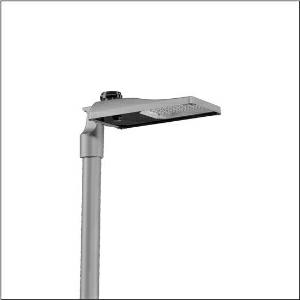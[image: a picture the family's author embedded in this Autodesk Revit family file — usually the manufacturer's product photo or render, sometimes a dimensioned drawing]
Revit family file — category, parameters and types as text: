
# Revit family: streetlight_sl_31_mini___st1_0a_5xh6d35m08ha_c080
name_source: partatom
category: Lighting Fixtures
units: mm (PartAtom-declared; Revit-internal decimal feet)

## family parameters
Cut with Voids When Loaded = No
Host = Face
Light Source = No
Part Type = Normal
Room Calculation Point = No
Round Connector Dimension = Use Diameter
Shared = No

## types (1)
- --- (1 x LED, 9230 lm, 68.3 W, 3000K)
    Apparent Load = 68 VA
    CIE Flux Codes = 37 72 97 100 100
    Color Rendering = 70
    Color Temperature = 3000K
    Default Elevation = 1800 mm
    Description = Streetlight SL 31 mini NEMA (7pin), Desk-Remote mast luminaire for post-top, side-entry; light control with lens of PMMA; light distribution: ST1.0a, direct asymmetric distribution, for standard-compliant lighting for roads and squares; LED: luminous flux: 9.230lm, light colour: 730, colour temperature: 3000K; luminous efficacy: 135,1lm/W; control: pre-setting: linear dimming characteristic, flexible luminous flux parameterisation, time-dependent luminous flux control, constant luminous flux control, intelligent temperature release in ECG and LED module, overheat protection; luminaire housing, of diecast aluminium, SITECO metallic grey (DB 702S), corrosivity category C5 high according to DIN EN ISO 12944; cover of toughened safety glass, transparent, opened without tools; mast flange of diecast aluminium, SITECO metallic grey (DB 702S), spigot size: 76/60mm, mast flange included unmounted; cable length: 8,5m, connection cable pre-assembled; mains connection: 220..240V, AC, 50/60Hz; power consumption (at start of service life): 68,3W / (at end of service life): 74,5W / (with reduced operation 50%): 29,5W; protection rating (complete): IP66; insulation class (complete): insulation class I (protective earthing); impact resistance: IK09; certification: CE, ENEC, ENEC+, VDE, UKCA; permissible operating ambient temperature for outdoor applications: -40..+50°C; packaging unit: 1 piece

Light Distribution: ST1.0a
    Height = 76 mm
    Lamp = 1 x LED
    Lamp Light Flux = 9230 lm
    Lamp Power = 68.3 W
    Lamp count = 1
    Length = 547 mm
    Luminous efficacy = 135 lm/W
    Manufacturer = Siteco
    ModVariant = No
    Model = 5XH6D35M08HA
    Number of Poles = 1
    OnlyDefault = Yes
    Power Factor = 1
    Product Name = Streetlight SL 31 mini | ST1.0a
    Product group = mast luminaire | pylon top
    ProductGroupID = 6100
    Protection Class = Protection class I
    Protection Degree = IP 66
    RLX_Detail_Level = 1
    RLX_Emergency_Light_Flux = 0 lm
    RLX_Emergency_Type = 0
    RLX_Emergency_Type_DB = No
    RlxData = <blob elided: 24757 chars, md5=ff9f1223>
    Socket = socket
    Standby Power = 0 W
    System Light Flux = 9230 lm
    System Power = 68 W
    Type Comments = factory setting: luminous flux: 100 % | dim-lin: 254 | 692 mA
    Type Image = l_1300324.jpg
    URL = http://relux.com
    VarID = @adj_020207
    Voltage = 0 V
    Weight = 0.00 kg
    Width = 265 mm

## geometry (parser evidence)
native form markers: Blend x4, Sweep x10
no freeform markers — native parametric forms only
